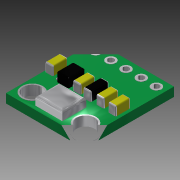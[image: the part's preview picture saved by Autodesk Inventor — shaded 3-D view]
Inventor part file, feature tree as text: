
AUTODESK INVENTOR PART (.ipt)
format: ipt  version: 2014 SP1 (Build 180222100, 222)  size: 464,896 bytes
history: native  units: mm
features: extrude x7, sketch x7, fillet x4, other x1
ambient origin geometry x8: Origin, YZ Plane, XZ Plane, XY Plane, X Axis, Y Axis, Z Axis, Center Point
bodies: Body1 (feature_tree)
feature tree (19):
  other  "Твердое тело1"
  extrude  "Выдавливание1"  Depth=13.1mm
  extrude  "Выдавливание2"  Depth=15.0mm
  extrude  "Выдавливание3"  Depth=3.0mm
  fillet  "Сопряжение1"  Radius=2.3mm
  fillet  "Сопряжение2"  Radius=2.3mm
  fillet  "Сопряжение3"  Radius=2.1mm
  extrude  "Выдавливание4"  Depth=2.1mm
  extrude  "Выдавливание6"  Depth=1.0mm
  extrude  "Выдавливание7"  Depth=1.5mm
  extrude  "Выдавливание8"  Depth=1.5mm
  fillet  "Сопряжение4"  Radius=2.54mm
  sketch  "Эскиз1"
  sketch  "Эскиз2"
  sketch  "Эскиз3"
  sketch  "Эскиз4"
  sketch  "Эскиз6"
  sketch  "Эскиз7"
  sketch  "Эскиз8"
